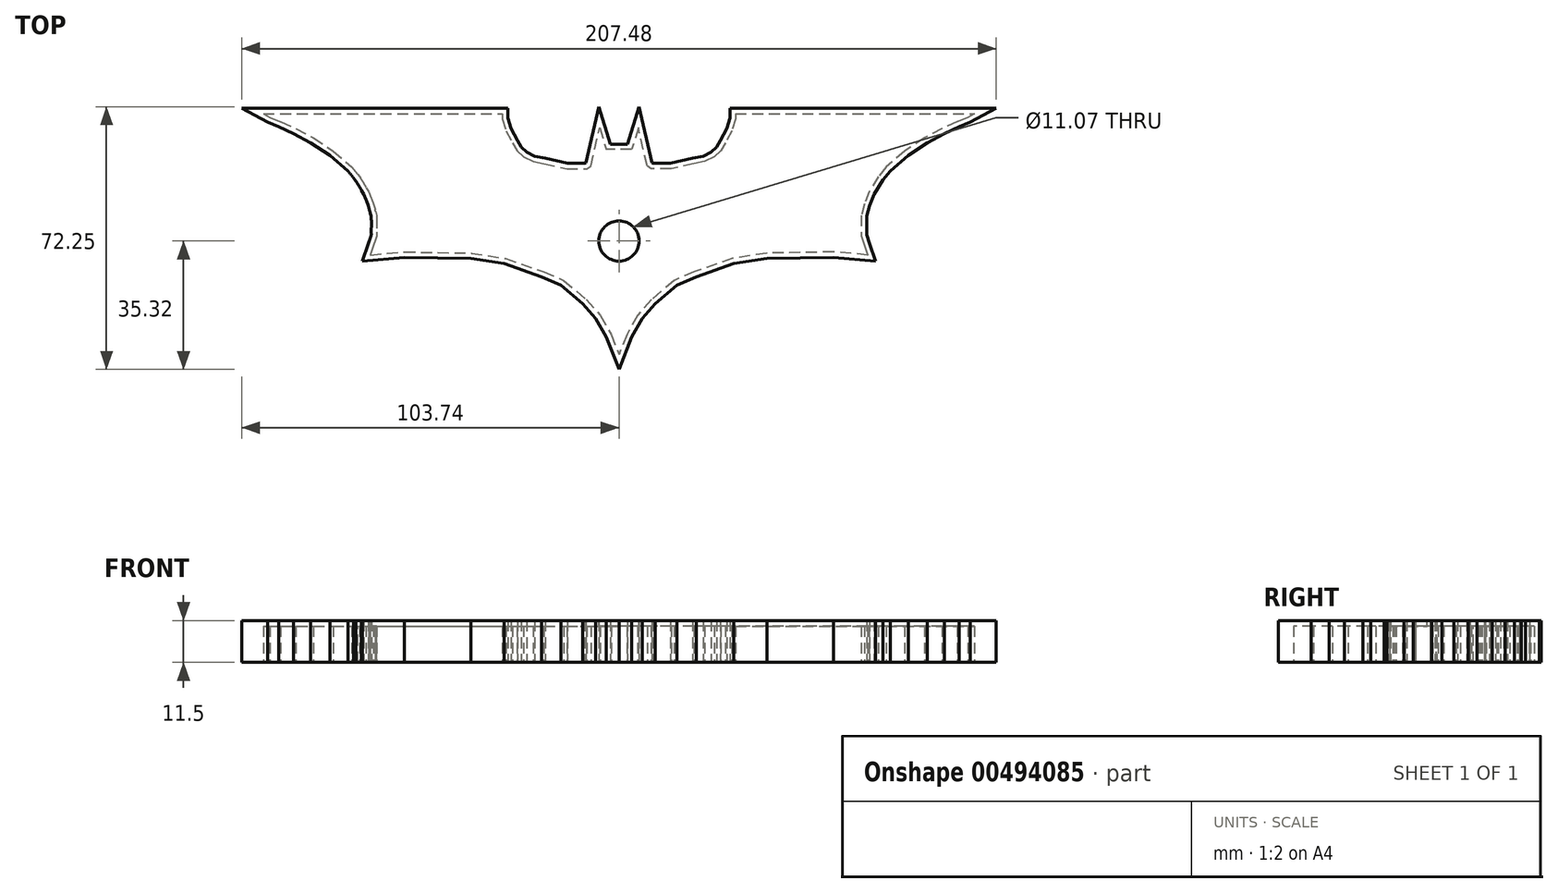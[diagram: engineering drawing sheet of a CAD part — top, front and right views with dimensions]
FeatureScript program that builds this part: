
annotation { "Feature Type Name" : "Feature", "Feature Type Description" : "" }
export const myFeature = defineFeature(function(context is Context, id is Id, definition is map)
    precondition{}
    {
        {
            var Q0;
            Q0=qCreatedBy(makeId("Top.planeOp"),FACE);
            var sketch = newSketch(context, id + "F0", { "sketchPlane" : qUnion([Q0])});
            skLineSegment(sketch, "E0", {"start": v(-97.13, 34.97) * mm, "end": v(-32.03, 34.97) * mm});
            skLineSegment(sketch, "E1", {"start": v(-32.03, 34.97) * mm, "end": v(-32.03, 33.59) * mm});
            skLineSegment(sketch, "E2", {"start": v(-32.03, 33.59) * mm, "end": v(-31.07, 30.32) * mm});
            skLineSegment(sketch, "E3", {"start": v(-31.07, 30.32) * mm, "end": v(-29.22, 26.9) * mm});
            skLineSegment(sketch, "E4", {"start": v(-29.22, 26.9) * mm, "end": v(-28, 24.85) * mm});
            skLineSegment(sketch, "E5", {"start": v(-28, 24.85) * mm, "end": v(-26.23, 23.14) * mm});
            skLineSegment(sketch, "E6", {"start": v(-26.23, 23.14) * mm, "end": v(-23.6, 21.86) * mm});
            skLineSegment(sketch, "E7", {"start": v(-23.6, 21.86) * mm, "end": v(-20.62, 21.3) * mm});
            skLineSegment(sketch, "E8", {"start": v(-20.62, 21.3) * mm, "end": v(-17.84, 20.65) * mm});
            skLineSegment(sketch, "E9", {"start": v(-17.84, 20.65) * mm, "end": v(-14.35, 19.84) * mm});
            skLineSegment(sketch, "E10", {"start": v(-14.35, 19.84) * mm, "end": v(-10.73, 19.84) * mm});
            skLineSegment(sketch, "E11", {"start": v(-10.73, 19.84) * mm, "end": v(-8.82, 19.84) * mm});
            skLineSegment(sketch, "E12", {"start": v(-8.82, 19.84) * mm, "end": v(-7.75, 20.65) * mm});
            skLineSegment(sketch, "E13", {"start": v(-7.75, 20.65) * mm, "end": v(-7.22, 22.96) * mm});
            skLineSegment(sketch, "E14", {"start": v(-7.22, 22.96) * mm, "end": v(-5.33, 31.14) * mm});
            skLineSegment(sketch, "E15", {"start": v(-5.33, 31.14) * mm, "end": v(-3.48, 25.13) * mm});
            skLineSegment(sketch, "E16", {"start": v(-3.48, 25.13) * mm, "end": v(0, 25.13) * mm});
            skLineSegment(sketch, "E17", {"start": v(-97.13, 34.97) * mm, "end": v(-97.75, 34.97) * mm});
            skLineSegment(sketch, "E18", {"start": v(-97.75, 34.97) * mm, "end": v(-95.94, 34) * mm});
            skLineSegment(sketch, "E19", {"start": v(-95.94, 34) * mm, "end": v(-92.98, 32.8) * mm});
            skLineSegment(sketch, "E20", {"start": v(-92.98, 32.8) * mm, "end": v(-88.85, 30.88) * mm});
            skLineSegment(sketch, "E21", {"start": v(-88.85, 30.88) * mm, "end": v(-84.03, 28.32) * mm});
            skLineSegment(sketch, "E22", {"start": v(-84.03, 28.32) * mm, "end": v(-78.6, 24.7) * mm});
            skLineSegment(sketch, "E23", {"start": v(-78.6, 24.7) * mm, "end": v(-73.47, 20.32) * mm});
            skLineSegment(sketch, "E24", {"start": v(-73.47, 20.32) * mm, "end": v(-71.35, 17.7) * mm});
            skLineSegment(sketch, "E25", {"start": v(-71.35, 17.7) * mm, "end": v(-68.82, 13.57) * mm});
            skLineSegment(sketch, "E26", {"start": v(-68.82, 13.57) * mm, "end": v(-67.46, 10.16) * mm});
            skLineSegment(sketch, "E27", {"start": v(-67.46, 10.16) * mm, "end": v(-66.62, 7.07) * mm});
            skLineSegment(sketch, "E28", {"start": v(-66.62, 7.07) * mm, "end": v(-66.62, 3.35) * mm});
            skLineSegment(sketch, "E29", {"start": v(-66.62, 3.35) * mm, "end": v(-66.62, 1.49) * mm});
            skLineSegment(sketch, "E30", {"start": v(-66.62, 1.49) * mm, "end": v(-67.46, -1.22) * mm});
            skLineSegment(sketch, "E31", {"start": v(-67.46, -1.22) * mm, "end": v(-68.4, -3.84) * mm});
            skLineSegment(sketch, "E32", {"start": v(-68.4, -3.84) * mm, "end": v(-59, -3) * mm});
            skLineSegment(sketch, "E33", {"start": v(-59, -3) * mm, "end": v(-40.58, -3.33) * mm});
            skLineSegment(sketch, "E34", {"start": v(-40.58, -3.33) * mm, "end": v(-31.2, -4.77) * mm});
            skLineSegment(sketch, "E35", {"start": v(-31.2, -4.77) * mm, "end": v(-20.68, -8.48) * mm});
            skLineSegment(sketch, "E36", {"start": v(-20.68, -8.48) * mm, "end": v(-15.18, -10.87) * mm});
            skLineSegment(sketch, "E37", {"start": v(-15.18, -10.87) * mm, "end": v(-8.97, -16.13) * mm});
            skLineSegment(sketch, "E38", {"start": v(-8.97, -16.13) * mm, "end": v(-5.14, -20.45) * mm});
            skLineSegment(sketch, "E39", {"start": v(-5.14, -20.45) * mm, "end": v(-2.15, -25.7) * mm});
            skLineSegment(sketch, "E40", {"start": v(-2.15, -25.7) * mm, "end": v(0, -31.2) * mm});
            skLineSegment(sketch, "E41.MirrorCS", {"start": v(66.62, 7.07) * mm, "end": v(66.62, 3.35) * mm});
            skLineSegment(sketch, "E42.MirrorCS", {"start": v(68.82, 13.57) * mm, "end": v(67.46, 10.16) * mm});
            skLineSegment(sketch, "E43.MirrorCS", {"start": v(8.82, 19.84) * mm, "end": v(7.75, 20.65) * mm});
            skLineSegment(sketch, "E44.MirrorCS", {"start": v(73.47, 20.32) * mm, "end": v(71.35, 17.7) * mm});
            skLineSegment(sketch, "E45.MirrorCS", {"start": v(15.18, -10.87) * mm, "end": v(8.97, -16.13) * mm});
            skLineSegment(sketch, "E46.MirrorCS", {"start": v(10.73, 19.84) * mm, "end": v(8.82, 19.84) * mm});
            skLineSegment(sketch, "E47.MirrorCS", {"start": v(14.35, 19.84) * mm, "end": v(10.73, 19.84) * mm});
            skLineSegment(sketch, "E48.MirrorCS", {"start": v(66.62, 1.49) * mm, "end": v(67.46, -1.22) * mm});
            skLineSegment(sketch, "E49.MirrorCS", {"start": v(88.85, 30.88) * mm, "end": v(84.03, 28.32) * mm});
            skLineSegment(sketch, "E50.MirrorCS", {"start": v(95.94, 34) * mm, "end": v(92.98, 32.8) * mm});
            skLineSegment(sketch, "E51.MirrorCS", {"start": v(97.13, 34.97) * mm, "end": v(97.75, 34.97) * mm});
            skLineSegment(sketch, "E52.MirrorCS", {"start": v(17.84, 20.65) * mm, "end": v(14.35, 19.84) * mm});
            skLineSegment(sketch, "E53.MirrorCS", {"start": v(20.62, 21.3) * mm, "end": v(17.84, 20.65) * mm});
            skLineSegment(sketch, "E54.MirrorCS", {"start": v(29.22, 26.9) * mm, "end": v(28, 24.85) * mm});
            skLineSegment(sketch, "E55.MirrorCS", {"start": v(31.07, 30.32) * mm, "end": v(29.22, 26.9) * mm});
            skLineSegment(sketch, "E56.MirrorCS", {"start": v(28, 24.85) * mm, "end": v(26.23, 23.14) * mm});
            skLineSegment(sketch, "E57.MirrorCS", {"start": v(97.75, 34.97) * mm, "end": v(95.94, 34) * mm});
            skLineSegment(sketch, "E58.MirrorCS", {"start": v(92.98, 32.8) * mm, "end": v(88.85, 30.88) * mm});
            skLineSegment(sketch, "E59.MirrorCS", {"start": v(66.62, 3.35) * mm, "end": v(66.62, 1.49) * mm});
            skLineSegment(sketch, "E60.MirrorCS", {"start": v(20.68, -8.48) * mm, "end": v(15.18, -10.87) * mm});
            skLineSegment(sketch, "E61.MirrorCS", {"start": v(32.03, 33.59) * mm, "end": v(31.07, 30.32) * mm});
            skLineSegment(sketch, "E62.MirrorCS", {"start": v(5.33, 31.14) * mm, "end": v(3.48, 25.13) * mm});
            skLineSegment(sketch, "E63.MirrorCS", {"start": v(7.75, 20.65) * mm, "end": v(7.22, 22.96) * mm});
            skLineSegment(sketch, "E64.MirrorCS", {"start": v(23.6, 21.86) * mm, "end": v(20.62, 21.3) * mm});
            skLineSegment(sketch, "E65.MirrorCS", {"start": v(8.97, -16.13) * mm, "end": v(5.14, -20.45) * mm});
            skLineSegment(sketch, "E66.MirrorCS", {"start": v(78.6, 24.7) * mm, "end": v(73.47, 20.32) * mm});
            skLineSegment(sketch, "E67.MirrorCS", {"start": v(5.14, -20.45) * mm, "end": v(2.15, -25.7) * mm});
            skLineSegment(sketch, "E68.MirrorCS", {"start": v(67.46, -1.22) * mm, "end": v(68.4, -3.84) * mm});
            skLineSegment(sketch, "E69.MirrorCS", {"start": v(84.03, 28.32) * mm, "end": v(78.6, 24.7) * mm});
            skLineSegment(sketch, "E70.MirrorCS", {"start": v(32.03, 34.97) * mm, "end": v(32.03, 33.59) * mm});
            skLineSegment(sketch, "E71.MirrorCS", {"start": v(71.35, 17.7) * mm, "end": v(68.82, 13.57) * mm});
            skLineSegment(sketch, "E72.MirrorCS", {"start": v(26.23, 23.14) * mm, "end": v(23.6, 21.86) * mm});
            skLineSegment(sketch, "E73.MirrorCS", {"start": v(67.46, 10.16) * mm, "end": v(66.62, 7.07) * mm});
            skLineSegment(sketch, "E74.MirrorCS", {"start": v(2.15, -25.7) * mm, "end": v(0, -31.2) * mm});
            skLineSegment(sketch, "E75.MirrorCS", {"start": v(31.2, -4.77) * mm, "end": v(20.68, -8.48) * mm});
            skLineSegment(sketch, "E76.MirrorCS", {"start": v(59, -3) * mm, "end": v(40.58, -3.33) * mm});
            skLineSegment(sketch, "E77.MirrorCS", {"start": v(40.58, -3.33) * mm, "end": v(31.2, -4.77) * mm});
            skLineSegment(sketch, "E78.MirrorCS", {"start": v(97.13, 34.97) * mm, "end": v(32.03, 34.97) * mm});
            skLineSegment(sketch, "E79.MirrorCS", {"start": v(7.22, 22.96) * mm, "end": v(5.33, 31.14) * mm});
            skLineSegment(sketch, "E80.MirrorCS", {"start": v(3.48, 25.13) * mm, "end": v(0, 25.13) * mm});
            skLineSegment(sketch, "E81.MirrorCS", {"start": v(68.4, -3.84) * mm, "end": v(59, -3) * mm});
            skFitSpline(sketch, "E82", {"points": [v(-73.47, 20.32) * mm, v(-71.1, 17.3) * mm, v(-69.48, 14.66) * mm, v(-68.14, 11.86) * mm, v(-67.04, 8.61) * mm, v(-66.62, 6.45) * mm, v(-66.62, 2.42) * mm], "startDerivative": vector(14.4, -16.93) * mm, "endDerivative": vector(-0.6, -23.65) * mm});
            skFitSpline(sketch, "E83", {"points": [v(-66.62, 2.42) * mm, v(-66.62, 1.49) * mm, v(-67.24, -0.5) * mm, v(-68.4, -3.84) * mm], "startDerivative": vector(0.6, -4.1) * mm, "endDerivative": vector(-2.72, -8.09) * mm});
            skSolve(sketch);
        }
        {
            var Q0;
            Q0=makeQuery(id+"F0.imprint","IMPRINT",FACE,{"disambiguationData":[TD([[makeQuery(id+"F0.imprint","IMPRINT",EDGE,{"derivedFrom":sQuery(id+"F0.wireOp",EDGE,"E0")}),-1.0]])]});
            extrude(context, id + "F1", {"entities" : qUnion([Q0]), "depth" : 10 * mm});
        }
        {
            var Q0;
            Q0=makeQuery(id+"F1.opExtrude","CAP_FACE",FACE,{"disambiguationData":[OSD([sQuery(id+"F0.wireOp",EDGE,"E0"),sQuery(id+"F0.wireOp",EDGE,"E1"),sQuery(id+"F0.wireOp",EDGE,"E2"),sQuery(id+"F0.wireOp",EDGE,"E3"),sQuery(id+"F0.wireOp",EDGE,"E4"),sQuery(id+"F0.wireOp",EDGE,"E5"),sQuery(id+"F0.wireOp",EDGE,"E6"),sQuery(id+"F0.wireOp",EDGE,"E7"),sQuery(id+"F0.wireOp",EDGE,"E8"),sQuery(id+"F0.wireOp",EDGE,"E9"),sQuery(id+"F0.wireOp",EDGE,"E10"),sQuery(id+"F0.wireOp",EDGE,"E11"),sQuery(id+"F0.wireOp",EDGE,"E12"),sQuery(id+"F0.wireOp",EDGE,"E13"),sQuery(id+"F0.wireOp",EDGE,"E14"),sQuery(id+"F0.wireOp",EDGE,"E15"),sQuery(id+"F0.wireOp",EDGE,"E16"),sQuery(id+"F0.wireOp",EDGE,"E17"),sQuery(id+"F0.wireOp",EDGE,"E18"),sQuery(id+"F0.wireOp",EDGE,"E19"),sQuery(id+"F0.wireOp",EDGE,"E20"),sQuery(id+"F0.wireOp",EDGE,"E21"),sQuery(id+"F0.wireOp",EDGE,"E22"),sQuery(id+"F0.wireOp",EDGE,"E23"),sQuery(id+"F0.wireOp",EDGE,"E24"),sQuery(id+"F0.wireOp",EDGE,"E25"),sQuery(id+"F0.wireOp",EDGE,"E26"),sQuery(id+"F0.wireOp",EDGE,"E27"),sQuery(id+"F0.wireOp",EDGE,"E28"),sQuery(id+"F0.wireOp",EDGE,"E30"),sQuery(id+"F0.wireOp",EDGE,"E31"),sQuery(id+"F0.wireOp",EDGE,"E32"),sQuery(id+"F0.wireOp",EDGE,"E33"),sQuery(id+"F0.wireOp",EDGE,"E34"),sQuery(id+"F0.wireOp",EDGE,"E35"),sQuery(id+"F0.wireOp",EDGE,"E36"),sQuery(id+"F0.wireOp",EDGE,"E37"),sQuery(id+"F0.wireOp",EDGE,"E38"),sQuery(id+"F0.wireOp",EDGE,"E39"),sQuery(id+"F0.wireOp",EDGE,"E40"),sQuery(id+"F0.wireOp",EDGE,"E41.MirrorCS"),sQuery(id+"F0.wireOp",EDGE,"E42.MirrorCS"),sQuery(id+"F0.wireOp",EDGE,"E43.MirrorCS"),sQuery(id+"F0.wireOp",EDGE,"E44.MirrorCS"),sQuery(id+"F0.wireOp",EDGE,"E45.MirrorCS"),sQuery(id+"F0.wireOp",EDGE,"E46.MirrorCS"),sQuery(id+"F0.wireOp",EDGE,"E47.MirrorCS"),sQuery(id+"F0.wireOp",EDGE,"E48.MirrorCS"),sQuery(id+"F0.wireOp",EDGE,"E49.MirrorCS"),sQuery(id+"F0.wireOp",EDGE,"E50.MirrorCS"),sQuery(id+"F0.wireOp",EDGE,"E51.MirrorCS"),sQuery(id+"F0.wireOp",EDGE,"E52.MirrorCS"),sQuery(id+"F0.wireOp",EDGE,"E53.MirrorCS"),sQuery(id+"F0.wireOp",EDGE,"E54.MirrorCS"),sQuery(id+"F0.wireOp",EDGE,"E55.MirrorCS"),sQuery(id+"F0.wireOp",EDGE,"E56.MirrorCS"),sQuery(id+"F0.wireOp",EDGE,"E57.MirrorCS"),sQuery(id+"F0.wireOp",EDGE,"E58.MirrorCS"),sQuery(id+"F0.wireOp",EDGE,"E59.MirrorCS"),sQuery(id+"F0.wireOp",EDGE,"E60.MirrorCS"),sQuery(id+"F0.wireOp",EDGE,"E61.MirrorCS"),sQuery(id+"F0.wireOp",EDGE,"E62.MirrorCS"),sQuery(id+"F0.wireOp",EDGE,"E63.MirrorCS"),sQuery(id+"F0.wireOp",EDGE,"E64.MirrorCS"),sQuery(id+"F0.wireOp",EDGE,"E65.MirrorCS"),sQuery(id+"F0.wireOp",EDGE,"E66.MirrorCS"),sQuery(id+"F0.wireOp",EDGE,"E67.MirrorCS"),sQuery(id+"F0.wireOp",EDGE,"E68.MirrorCS"),sQuery(id+"F0.wireOp",EDGE,"E69.MirrorCS"),sQuery(id+"F0.wireOp",EDGE,"E70.MirrorCS"),sQuery(id+"F0.wireOp",EDGE,"E71.MirrorCS"),sQuery(id+"F0.wireOp",EDGE,"E72.MirrorCS"),sQuery(id+"F0.wireOp",EDGE,"E73.MirrorCS"),sQuery(id+"F0.wireOp",EDGE,"E74.MirrorCS"),sQuery(id+"F0.wireOp",EDGE,"E75.MirrorCS"),sQuery(id+"F0.wireOp",EDGE,"E76.MirrorCS"),sQuery(id+"F0.wireOp",EDGE,"E77.MirrorCS"),sQuery(id+"F0.wireOp",EDGE,"E78.MirrorCS"),sQuery(id+"F0.wireOp",EDGE,"E79.MirrorCS"),sQuery(id+"F0.wireOp",EDGE,"E80.MirrorCS"),sQuery(id+"F0.wireOp",EDGE,"E81.MirrorCS"),sQuery(id+"F0.wireOp",EDGE,"E82"),sQuery(id+"F0.wireOp",EDGE,"E83")])],"isStart":true});
            shell(context, id + "F2", {"entities" : qUnion([Q0]), "thickness" : 1.5 * mm, "oppositeDirection" : true});
        }
        {
            var Q0;
            Q0=makeQuery(id+"F1.opExtrude","CAP_FACE",FACE,{"disambiguationData":[OSD([sQuery(id+"F0.wireOp",EDGE,"E0"),sQuery(id+"F0.wireOp",EDGE,"E1"),sQuery(id+"F0.wireOp",EDGE,"E2"),sQuery(id+"F0.wireOp",EDGE,"E3"),sQuery(id+"F0.wireOp",EDGE,"E4"),sQuery(id+"F0.wireOp",EDGE,"E5"),sQuery(id+"F0.wireOp",EDGE,"E6"),sQuery(id+"F0.wireOp",EDGE,"E7"),sQuery(id+"F0.wireOp",EDGE,"E8"),sQuery(id+"F0.wireOp",EDGE,"E9"),sQuery(id+"F0.wireOp",EDGE,"E10"),sQuery(id+"F0.wireOp",EDGE,"E11"),sQuery(id+"F0.wireOp",EDGE,"E12"),sQuery(id+"F0.wireOp",EDGE,"E13"),sQuery(id+"F0.wireOp",EDGE,"E14"),sQuery(id+"F0.wireOp",EDGE,"E15"),sQuery(id+"F0.wireOp",EDGE,"E16"),sQuery(id+"F0.wireOp",EDGE,"E17"),sQuery(id+"F0.wireOp",EDGE,"E18"),sQuery(id+"F0.wireOp",EDGE,"E19"),sQuery(id+"F0.wireOp",EDGE,"E20"),sQuery(id+"F0.wireOp",EDGE,"E21"),sQuery(id+"F0.wireOp",EDGE,"E22"),sQuery(id+"F0.wireOp",EDGE,"E23"),sQuery(id+"F0.wireOp",EDGE,"E24"),sQuery(id+"F0.wireOp",EDGE,"E25"),sQuery(id+"F0.wireOp",EDGE,"E26"),sQuery(id+"F0.wireOp",EDGE,"E27"),sQuery(id+"F0.wireOp",EDGE,"E28"),sQuery(id+"F0.wireOp",EDGE,"E30"),sQuery(id+"F0.wireOp",EDGE,"E31"),sQuery(id+"F0.wireOp",EDGE,"E32"),sQuery(id+"F0.wireOp",EDGE,"E33"),sQuery(id+"F0.wireOp",EDGE,"E34"),sQuery(id+"F0.wireOp",EDGE,"E35"),sQuery(id+"F0.wireOp",EDGE,"E36"),sQuery(id+"F0.wireOp",EDGE,"E37"),sQuery(id+"F0.wireOp",EDGE,"E38"),sQuery(id+"F0.wireOp",EDGE,"E39"),sQuery(id+"F0.wireOp",EDGE,"E40"),sQuery(id+"F0.wireOp",EDGE,"E41.MirrorCS"),sQuery(id+"F0.wireOp",EDGE,"E42.MirrorCS"),sQuery(id+"F0.wireOp",EDGE,"E43.MirrorCS"),sQuery(id+"F0.wireOp",EDGE,"E44.MirrorCS"),sQuery(id+"F0.wireOp",EDGE,"E45.MirrorCS"),sQuery(id+"F0.wireOp",EDGE,"E46.MirrorCS"),sQuery(id+"F0.wireOp",EDGE,"E47.MirrorCS"),sQuery(id+"F0.wireOp",EDGE,"E48.MirrorCS"),sQuery(id+"F0.wireOp",EDGE,"E49.MirrorCS"),sQuery(id+"F0.wireOp",EDGE,"E50.MirrorCS"),sQuery(id+"F0.wireOp",EDGE,"E51.MirrorCS"),sQuery(id+"F0.wireOp",EDGE,"E52.MirrorCS"),sQuery(id+"F0.wireOp",EDGE,"E53.MirrorCS"),sQuery(id+"F0.wireOp",EDGE,"E54.MirrorCS"),sQuery(id+"F0.wireOp",EDGE,"E55.MirrorCS"),sQuery(id+"F0.wireOp",EDGE,"E56.MirrorCS"),sQuery(id+"F0.wireOp",EDGE,"E57.MirrorCS"),sQuery(id+"F0.wireOp",EDGE,"E58.MirrorCS"),sQuery(id+"F0.wireOp",EDGE,"E59.MirrorCS"),sQuery(id+"F0.wireOp",EDGE,"E60.MirrorCS"),sQuery(id+"F0.wireOp",EDGE,"E61.MirrorCS"),sQuery(id+"F0.wireOp",EDGE,"E62.MirrorCS"),sQuery(id+"F0.wireOp",EDGE,"E63.MirrorCS"),sQuery(id+"F0.wireOp",EDGE,"E64.MirrorCS"),sQuery(id+"F0.wireOp",EDGE,"E65.MirrorCS"),sQuery(id+"F0.wireOp",EDGE,"E66.MirrorCS"),sQuery(id+"F0.wireOp",EDGE,"E67.MirrorCS"),sQuery(id+"F0.wireOp",EDGE,"E68.MirrorCS"),sQuery(id+"F0.wireOp",EDGE,"E69.MirrorCS"),sQuery(id+"F0.wireOp",EDGE,"E70.MirrorCS"),sQuery(id+"F0.wireOp",EDGE,"E71.MirrorCS"),sQuery(id+"F0.wireOp",EDGE,"E72.MirrorCS"),sQuery(id+"F0.wireOp",EDGE,"E73.MirrorCS"),sQuery(id+"F0.wireOp",EDGE,"E74.MirrorCS"),sQuery(id+"F0.wireOp",EDGE,"E75.MirrorCS"),sQuery(id+"F0.wireOp",EDGE,"E76.MirrorCS"),sQuery(id+"F0.wireOp",EDGE,"E77.MirrorCS"),sQuery(id+"F0.wireOp",EDGE,"E78.MirrorCS"),sQuery(id+"F0.wireOp",EDGE,"E79.MirrorCS"),sQuery(id+"F0.wireOp",EDGE,"E80.MirrorCS"),sQuery(id+"F0.wireOp",EDGE,"E81.MirrorCS"),sQuery(id+"F0.wireOp",EDGE,"E82"),sQuery(id+"F0.wireOp",EDGE,"E83")])],"isStart":false});
            var sketch = newSketch(context, id + "F3", { "sketchPlane" : qUnion([Q0])});
            skCircle(sketch, "E84", {"center": v(0, 0) * mm, "radius": 5.54 * mm});
            skSolve(sketch);
        }
        {
            var Q0;
            Q0 = qSketchRegion(id + "F3", true);
            extrude(context, id + "F4", {"entities" : qUnion([Q0]), "operationType" : NewBodyOperationType.REMOVE, "oppositeDirection" : true, "depth" : 25 * mm});
        }
    });
